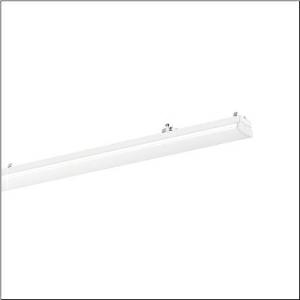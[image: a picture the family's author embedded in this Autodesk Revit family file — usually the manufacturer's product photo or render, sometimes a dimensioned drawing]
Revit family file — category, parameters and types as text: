
# Revit family: licross_21_recessed_opal_mo_52te1ddn445g
name_source: partatom
category: Lighting Fixtures
units: mm (PartAtom-declared; Revit-internal decimal feet)

## family parameters
Cut with Voids When Loaded = No
Host = Face
Light Source = No
Part Type = Normal
Room Calculation Point = No
Round Connector Dimension = Use Diameter
Shared = No

## types (1)
- --- (1 x LED, 4500 lm, 25.8 W, 4000K)
    Apparent Load = 26 VA
    CIE Flux Codes = 44 73 91 87 100
    Color Rendering = 80
    Color Temperature = 4000K
    Default Elevation = 1800 mm
    Description = Licross 21 recessed opal MO, luminaire insert, of sheet steel, galvanised, coil coated, white, length: 1.500mm, width: 66mm, height: 67mm, LED rated luminous flux: 4.500lm, light colour: 840, SDCM (Standard Deviation of Colour Matching)MacAdam ≤ 3 SDCM (initial), control gear: DALI 2, with plug, 5-pole, with phase selection, mains connection: 220..240V, AC, 50/60Hz, rated input power: 26W, internal wiring halogen-free, primary optical cover: cover, of PMMA, light emission: direct with ceiling illumination distribution, primary light characteristic: symmetric, protection rating (complete): IP54, insulation class (complete): insulation class I (protective earthing), certification: CE, ENEC, VDE, UKCA, protection symbol: D if used in an environment with non-conductive dust loads with corresponding accessories, impact resistance: IK06, permissible ambient temperature for indoor applications: -25..+45°C, corresponds to IFS (International Featured Standards) requirements for safety and quality in the food industry, reducing of maximum allowable ambient temperature of 5°C with ceiling mounting, LABS conformity tested according to VDMA 24364:2018-05, The light source and the operating device comply with the requirements of the Ecodesign Regulation (EU) 2019/2020 and are replaceable in accordance with this regulation, packaging unit: 1 piece
    Height = 83 mm
    Lamp = 1 x LED
    Lamp Light Flux = 4500 lm
    Lamp Power = 25.8 W
    Lamp count = 1
    Length = 1500 mm
    Luminous efficacy = 174 lm/W
    Manufacturer = Siteco
    ModVariant = No
    Model = 52TE1DDN445G
    Mounting Place = Ceiling
    Mounting Type = Pendant
    Number of Poles = 1
    OnlyDefault = Yes
    Power Factor = 1
    Product Name = Licross 21 recessed opal MO
    Product group = luminaire insert | ceiling pendant
    ProductGroupID = 901
    Protection Class = Protection class I
    Protection Degree = IP 54
    RLX_Detail_Level = 1
    RLX_Emergency_Light_Flux = 0 lm
    RLX_Emergency_Type = 0
    RLX_Emergency_Type_DB = No
    RlxData = <blob elided: 26565 chars, md5=0d22ade9>
    Socket = socket
    Standby Power = 0 W
    System Light Flux = 4500 lm
    System Power = 26 W
    Type Comments = factory setting: luminous flux: 100 % | dim-lin: 254 | 172 mA
    Type Image = l_1313666.jpg
    URL = http://relux.com
    VarID = @adj_070767
    Voltage = 0 V
    Weight = 0.00 kg
    Width = 76 mm

## geometry (parser evidence)
native form markers: Blend x4, Sweep x12
no freeform markers — native parametric forms only
